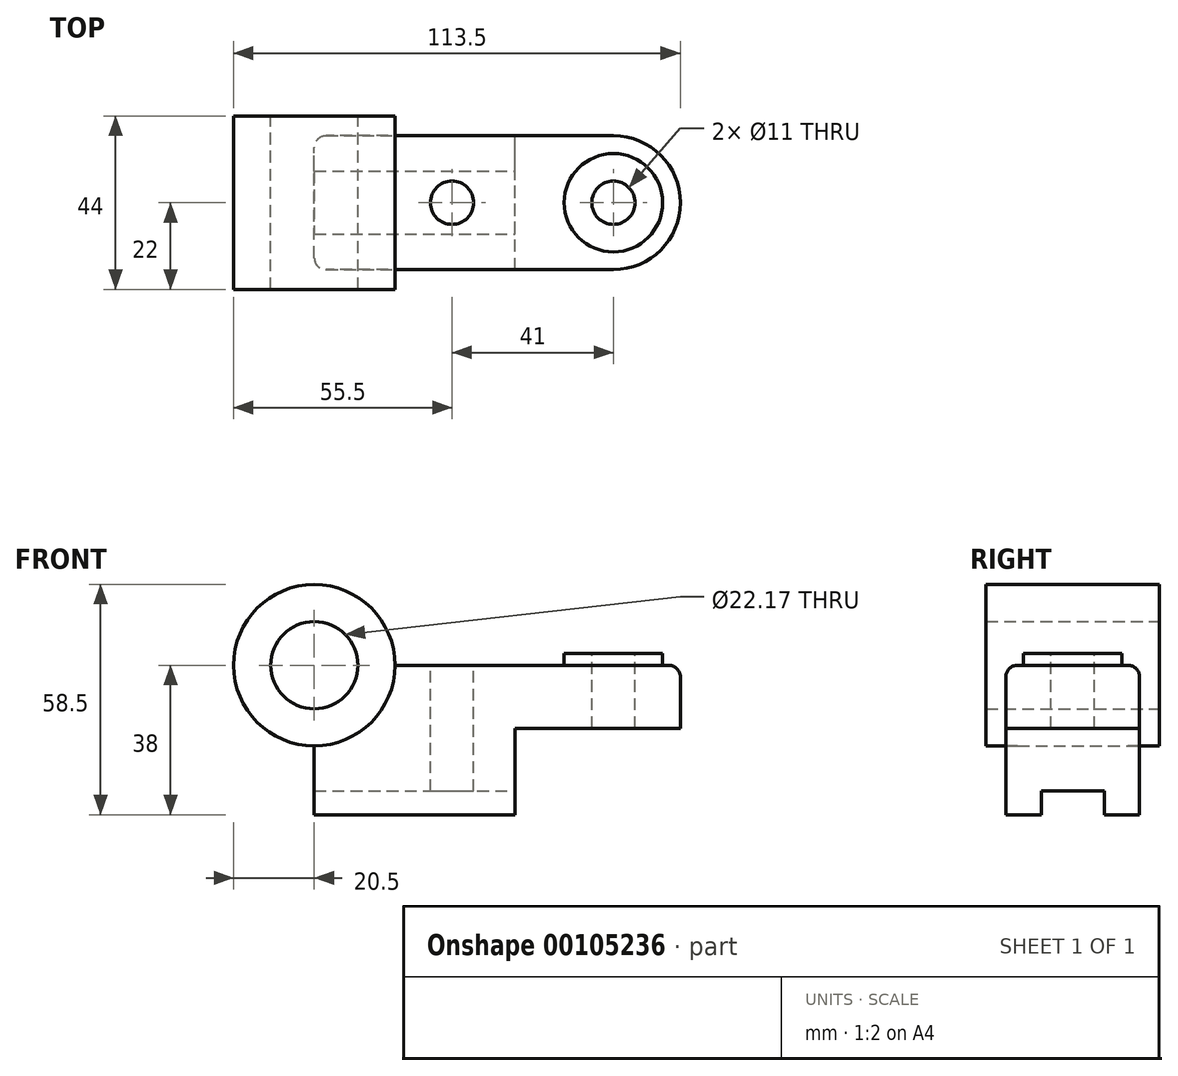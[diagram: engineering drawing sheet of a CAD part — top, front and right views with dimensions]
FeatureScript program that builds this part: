
annotation { "Feature Type Name" : "Feature", "Feature Type Description" : "" }
export const myFeature = defineFeature(function(context is Context, id is Id, definition is map)
    precondition{}
    {
        {
            var Q0;
            Q0=qCreatedBy(makeId("Front.planeOp"),FACE);
            var sketch = newSketch(context, id + "F0", { "sketchPlane" : qUnion([Q0])});
            skLineSegment(sketch, "E0.top", {"start": v(0, 38) * mm, "end": v(76, 38) * mm});
            skLineSegment(sketch, "E0.left", {"start": v(0, 0) * mm, "end": v(0, 38) * mm});
            skLineSegment(sketch, "E1.top", {"start": v(76, 22) * mm, "end": v(51, 22) * mm});
            skLineSegment(sketch, "E1.right", {"start": v(51, 0) * mm, "end": v(51, 22) * mm});
            skCircle(sketch, "E2", {"center": v(0, 38) * mm, "radius": 11.09 * mm});
            skCircle(sketch, "E3", {"center": v(0, 38) * mm, "radius": 20.5 * mm});
            skLineSegment(sketch, "E4", {"start": v(76, 38) * mm, "end": v(76, 22) * mm});
            skLineSegment(sketch, "E5", {"start": v(51, 0) * mm, "end": v(0, 0) * mm});
            skSolve(sketch);
        }
        {
            var Q0;
            Q0=makeQuery(id+"F0.imprint","IMPRINT",FACE,{"disambiguationData":[TD([[makeQuery(id+"F0.imprint","IMPRINT",EDGE,{"derivedFrom":sQuery(id+"F0.wireOp",EDGE,"E1.top")}),-1.0]])]});
            extrude(context, id + "F1", {"entities" : qUnion([Q0]), "endBound" : BoundingType.SYMMETRIC, "depth" : 34 * mm});
        }
        {
            var Q0;
            {var subQ0=sQuery(id+"F0.wireOp",EDGE,"E3");var subQ1=sQuery(id+"F0.wireOp",EDGE,"E0.top");var subQ2=makeQuery(id+"F0.imprint","INTERSECT",VERTEX,{"derivedFrom":[subQ1,subQ0]});Q0=makeQuery(id+"F0.imprint","IMPRINT",FACE,{"disambiguationData":[TD([[makeQuery(id+"F0.imprint","IMPRINT",EDGE,{"disambiguationData":[TD([[subQ2,1.0]])],"derivedFrom":subQ1}),1.0]])]});}
            var Q1;
            {var subQ0=sQuery(id+"F0.wireOp",EDGE,"E3");var subQ1=sQuery(id+"F0.wireOp",EDGE,"E0.top");var subQ2=makeQuery(id+"F0.imprint","INTERSECT",VERTEX,{"derivedFrom":[subQ1,subQ0]});Q1=makeQuery(id+"F0.imprint","IMPRINT",FACE,{"disambiguationData":[TD([[makeQuery(id+"F0.imprint","IMPRINT",EDGE,{"disambiguationData":[TD([[subQ2,1.0]])],"derivedFrom":subQ1}),-1.0]])]});}
            extrude(context, id + "F2", {"entities" : qUnion([Q0, Q1]), "operationType" : NewBodyOperationType.ADD, "endBound" : BoundingType.SYMMETRIC, "depth" : 44 * mm});
        }
        {
            var Q0;
            Q0=makeQuery(id+"F1.opExtrude","SWEPT_FACE",FACE,{"disambiguationData":[OSD([sQuery(id+"F0.wireOp",EDGE,"E0.top")])]});
            var sketch = newSketch(context, id + "F3", { "sketchPlane" : qUnion([Q0])});
            skArc(sketch, "E6", {"start": v(76, -17) * mm, "mid": v(93, 0) * mm, "end": v(76, 17) * mm});
            skSolve(sketch);
        }
        {
            var Q0;
            Q0=makeQuery(id+"F3.imprint","IMPRINT",FACE,{"disambiguationData":[TD([[makeQuery(id+"F3.imprint","IMPRINT",EDGE,{"derivedFrom":sQuery(id+"F3.wireOp",EDGE,"E6")}),1.0]])]});
            var Q1;
            Q1=makeQuery(id+"F1.opExtrude","SWEPT_FACE",FACE,{"disambiguationData":[OSD([sQuery(id+"F0.wireOp",EDGE,"E1.top")])]});
            extrude(context, id + "F4", {"entities" : qUnion([Q0]), "operationType" : NewBodyOperationType.ADD, "endBound" : BoundingType.UP_TO_SURFACE, "oppositeDirection" : true, "endBoundEntityFace" : qUnion([Q1]), "depth" : 25 * mm});
        }
        {
            var Q0;
            {var subQ0=sQuery(id+"F0.wireOp",EDGE,"E0.top");Q0=makeQuery(id+"F3.imprint","IMPRINT",FACE,{"disambiguationData":[TD([[makeQuery(id+"F3.imprint","IMPRINT",EDGE,{"derivedFrom":makeQuery(id+"F1.opExtrude","CAP_EDGE",EDGE,{"disambiguationData":[OSD([subQ0])],"isStart":true})}),-1.0]])]});}
            var sketch = newSketch(context, id + "F5", { "sketchPlane" : qUnion([Q0])});
            skCircle(sketch, "E7", {"center": v(76, 0) * mm, "radius": 12.5 * mm});
            skSolve(sketch);
        }
        {
            var Q0;
            {var subQ0=sQuery(id+"F5.wireOp",EDGE,"E7");var subQ1=makeQuery(id+"F3.imprint","IMPRINT",EDGE,{"derivedFrom":makeQuery(id+"F1.opExtrude","SWEPT_EDGE",EDGE,{"disambiguationData":[OSD([sQuery(id+"F0.wireOp",EDGE,"E0.top"),sQuery(id+"F0.wireOp",EDGE,"E4")])]})});var subQ2=makeQuery(id+"F5.imprint","INTERSECT",VERTEX,{"disambiguationData":[OD(0.0)],"derivedFrom":[subQ1,subQ0]});Q0=makeQuery(id+"F5.imprint","IMPRINT",FACE,{"disambiguationData":[TD([[makeQuery(id+"F5.imprint","IMPRINT",EDGE,{"disambiguationData":[TD([[subQ2,1.0]])],"derivedFrom":subQ0}),1.0]])]});}
            var Q1;
            {var subQ0=sQuery(id+"F5.wireOp",EDGE,"E7");var subQ1=makeQuery(id+"F3.imprint","IMPRINT",EDGE,{"derivedFrom":makeQuery(id+"F1.opExtrude","SWEPT_EDGE",EDGE,{"disambiguationData":[OSD([sQuery(id+"F0.wireOp",EDGE,"E0.top"),sQuery(id+"F0.wireOp",EDGE,"E4")])]})});var subQ2=makeQuery(id+"F5.imprint","INTERSECT",VERTEX,{"disambiguationData":[OD(0.0)],"derivedFrom":[subQ1,subQ0]});Q1=makeQuery(id+"F5.imprint","IMPRINT",FACE,{"disambiguationData":[TD([[makeQuery(id+"F5.imprint","IMPRINT",EDGE,{"disambiguationData":[TD([[subQ2,-1.0]])],"derivedFrom":subQ0}),1.0]])]});}
            extrude(context, id + "F6", {"entities" : qUnion([Q0, Q1]), "operationType" : NewBodyOperationType.ADD, "depth" : 3 * mm});
        }
        {
            var Q0;
            Q0=makeQuery(id+"F6.opExtrude","CAP_FACE",FACE,{"disambiguationData":[OSD([sQuery(id+"F5.wireOp",EDGE,"E7")])],"isStart":false});
            var sketch = newSketch(context, id + "F7", { "sketchPlane" : qUnion([Q0])});
            skCircle(sketch, "E8", {"center": v(76, 0) * mm, "radius": 5.5 * mm});
            skCircle(sketch, "E9", {"center": v(35, 0) * mm, "radius": 5.5 * mm});
            skSolve(sketch);
        }
        {
            var Q0;
            Q0=makeQuery(id+"F7.imprint","IMPRINT",FACE,{"disambiguationData":[TD([[makeQuery(id+"F7.imprint","IMPRINT",EDGE,{"derivedFrom":sQuery(id+"F7.wireOp",EDGE,"E9")}),1.0]])]});
            var Q1;
            Q1=makeQuery(id+"F7.imprint","IMPRINT",FACE,{"disambiguationData":[TD([[makeQuery(id+"F7.imprint","IMPRINT",EDGE,{"derivedFrom":sQuery(id+"F7.wireOp",EDGE,"E8")}),1.0]])]});
            extrude(context, id + "F8", {"entities" : qUnion([Q0, Q1]), "operationType" : NewBodyOperationType.REMOVE, "endBound" : BoundingType.THROUGH_ALL, "oppositeDirection" : true, "depth" : 25 * mm});
        }
        {
            var Q0;
            Q0=makeQuery(id+"F1.opExtrude","SWEPT_FACE",FACE,{"disambiguationData":[OSD([sQuery(id+"F0.wireOp",EDGE,"E1.right")])]});
            var sketch = newSketch(context, id + "F9", { "sketchPlane" : qUnion([Q0])});
            skLineSegment(sketch, "E10.bottom", {"start": v(-8, 0) * mm, "end": v(8, 0) * mm});
            skLineSegment(sketch, "E10.top", {"start": v(-8, 6) * mm, "end": v(8, 6) * mm});
            skLineSegment(sketch, "E10.left", {"start": v(-8, 0) * mm, "end": v(-8, 6) * mm});
            skLineSegment(sketch, "E10.right", {"start": v(8, 0) * mm, "end": v(8, 6) * mm});
            skSolve(sketch);
        }
        {
            var Q0;
            Q0=makeQuery(id+"F9.imprint","IMPRINT",FACE,{"disambiguationData":[TD([[makeQuery(id+"F9.imprint","IMPRINT",EDGE,{"derivedFrom":sQuery(id+"F9.wireOp",EDGE,"E10.bottom")}),1.0]])]});
            extrude(context, id + "F10", {"entities" : qUnion([Q0]), "operationType" : NewBodyOperationType.REMOVE, "endBound" : BoundingType.THROUGH_ALL, "oppositeDirection" : true, "depth" : 25 * mm});
        }
        {
            var Q0;
            Q0=makeQuery(id+"F6.opExtrude","CAP_EDGE",EDGE,{"disambiguationData":[OSD([sQuery(id+"F5.wireOp",EDGE,"E7")])],"isStart":true});
            var Q1;
            Q1=makeQuery(id+"F1.opExtrude","SWEPT_EDGE",EDGE,{"disambiguationData":[OSD([sQuery(id+"F0.wireOp",EDGE,"E0.top"),sQuery(id+"F0.wireOp",EDGE,"E3")])]});
            var Q2;
            Q2=makeQuery(id+"F1.opExtrude","CAP_EDGE",EDGE,{"disambiguationData":[OSD([sQuery(id+"F0.wireOp",EDGE,"E3")])],"isStart":false});
            var Q3;
            Q3=makeQuery(id+"F1.opExtrude","CAP_EDGE",EDGE,{"disambiguationData":[OSD([sQuery(id+"F0.wireOp",EDGE,"E3")])],"isStart":true});
            var Q4;
            Q4=makeQuery(id+"F1.opExtrude","CAP_EDGE",EDGE,{"disambiguationData":[OSD([sQuery(id+"F0.wireOp",EDGE,"E0.left")])],"isStart":true});
            var Q5;
            Q5=makeQuery(id+"F1.opExtrude","CAP_EDGE",EDGE,{"disambiguationData":[OSD([sQuery(id+"F0.wireOp",EDGE,"E0.left")])],"isStart":false});
            fillet(context, id + "F11", {"entities" : qUnion([Q0, Q1, Q2, Q3, Q4, Q5]), "radius" : 3 * mm, "tangentPropagation" : true, "allowEdgeOverflow" : false});
        }
        {
            var Q0;
            Q0=makeQuery(id+"F1.opExtrude","CAP_EDGE",EDGE,{"disambiguationData":[OSD([sQuery(id+"F0.wireOp",EDGE,"E0.top")])],"isStart":false});
            fillet(context, id + "F12", {"entities" : qUnion([Q0]), "radius" : 3 * mm, "tangentPropagation" : true, "allowEdgeOverflow" : false});
        }
    });
